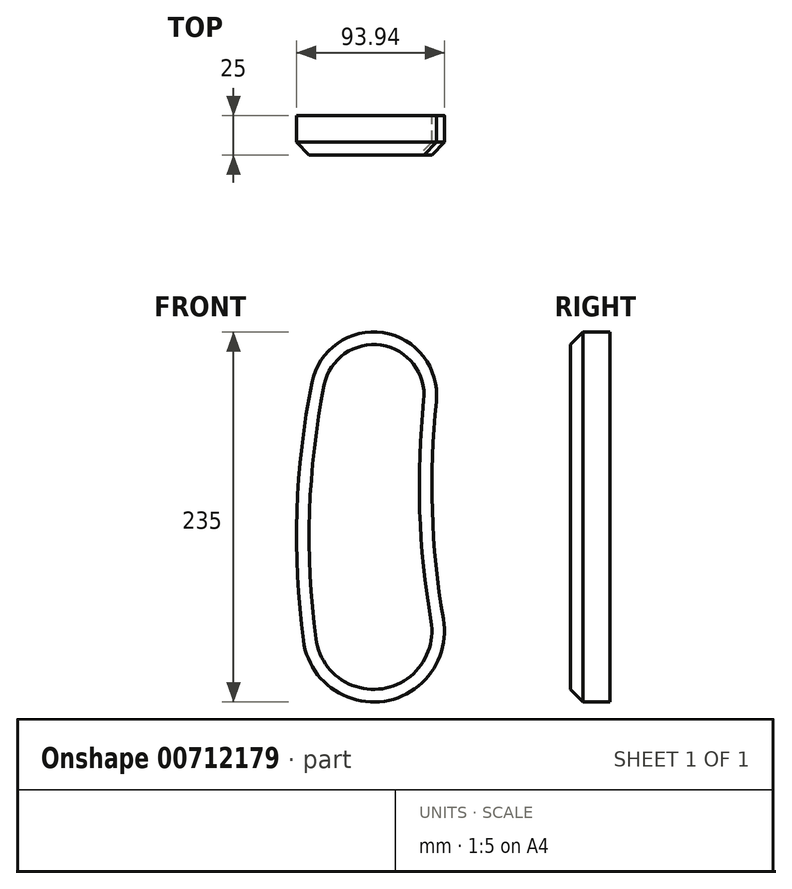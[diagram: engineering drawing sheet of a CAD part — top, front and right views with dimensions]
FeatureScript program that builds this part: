
annotation { "Feature Type Name" : "Feature", "Feature Type Description" : "" }
export const myFeature = defineFeature(function(context is Context, id is Id, definition is map)
    precondition{}
    {
        {
            var Q0;
            Q0=qCreatedBy(makeId("Front.planeOp"),FACE);
            var sketch = newSketch(context, id + "F0", { "sketchPlane" : qUnion([Q0])});
            skArc(sketch, "E0", {"start": v(39.78, -4.22) * mm, "mid": v(6.04, 39.54) * mm, "end": v(-39.22, 7.85) * mm});
            skLineSegment(sketch, "E1", {"start": v(0, 0) * mm, "end": v(0, -150) * mm, "construction": true});
            skArc(sketch, "E2", {"start": v(-44.61, -155.9) * mm, "mid": v(6.8, -194.48) * mm, "end": v(44.34, -142.31) * mm});
            skArc(sketch, "E3", {"start": v(-39.22, 7.85) * mm, "mid": v(-48.67, -73.8) * mm, "end": v(-44.61, -155.9) * mm});
            skArc(sketch, "E4", {"start": v(39.78, -4.22) * mm, "mid": v(37.26, -73.42) * mm, "end": v(44.34, -142.31) * mm});
            skSolve(sketch);
        }
        {
            var Q0;
            Q0 = qSketchRegion(id + "F0", true);
            extrude(context, id + "F1", {"entities" : qUnion([Q0]), "depth" : 25 * mm, "offsetDistance" : 25 * mm});
        }
        {
            var Q0;
            Q0=makeQuery(id+"F1.opExtrude","CAP_EDGE",EDGE,{"disambiguationData":[OSD([sQuery(id+"F0.wireOp",EDGE,"E0")])],"isStart":false});
            chamfer(context, id + "F2", {"entities" : qUnion([Q0]), "width" : 8 * mm, "tangentPropagation" : true});
        }
    });
